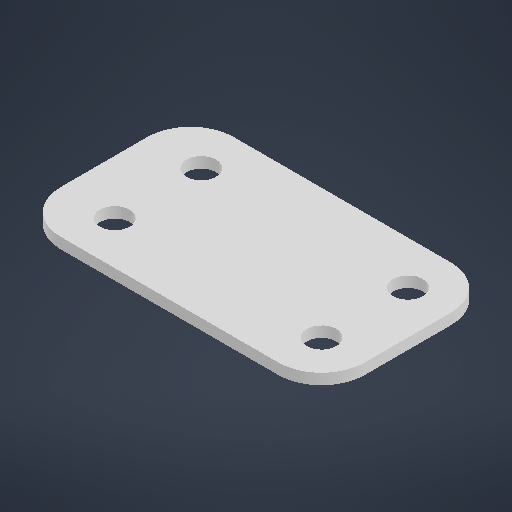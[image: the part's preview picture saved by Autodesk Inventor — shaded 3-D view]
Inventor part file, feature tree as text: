
AUTODESK INVENTOR PART (.ipt)
format: ipt  version: 2025.2 (Build 292293000, 293)  size: 191,488 bytes
history: native  units: in
note: dims shown in document units (in); Inventor stores cm internally (conversion verified against a paired STEP export)
features: extrude x1, sketch x1
ambient origin geometry x8: Origin, YZ Plane, XZ Plane, XY Plane, X Axis, Y Axis, Z Axis, Center Point
bodies: Solid1 (feature_tree)
feature tree (2):
  extrude  "Extrusion1"  Depth=0.0625in
  sketch  "Sketch1"  dims[d0=0.172in d2=0.172in d4=0.172in d5=0.172in d8=0.5in d9=0.5in d10=0.0625in d12=0.5in d13=0.5in d14=0.0625in d15=0.0in]
